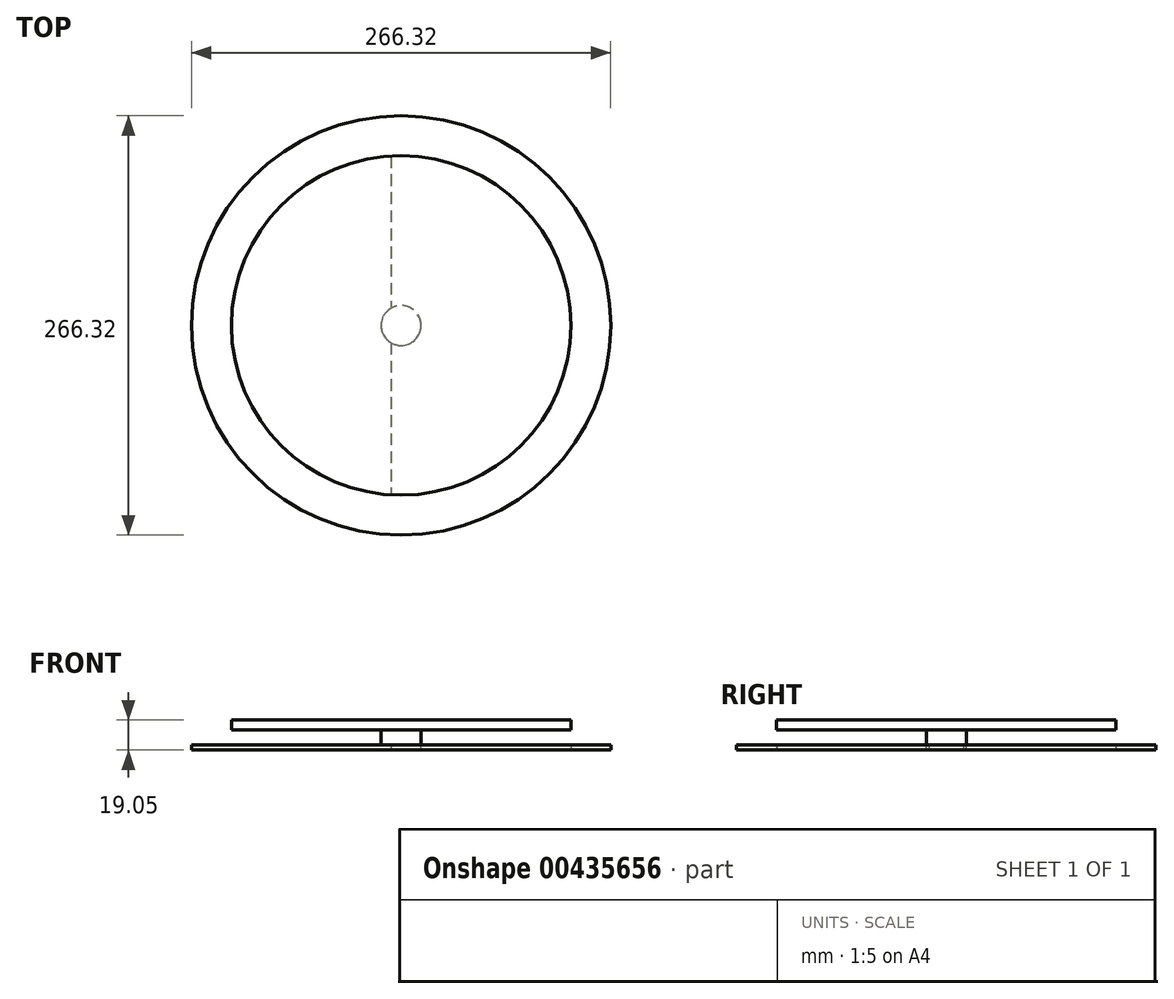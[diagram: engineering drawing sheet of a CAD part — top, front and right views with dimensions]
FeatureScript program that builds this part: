
annotation { "Feature Type Name" : "Feature", "Feature Type Description" : "" }
export const myFeature = defineFeature(function(context is Context, id is Id, definition is map)
    precondition{}
    {
        {
            var Q0;
            Q0=qCreatedBy(makeId("Top.planeOp"),FACE);
            var sketch = newSketch(context, id + "F0", { "sketchPlane" : qUnion([Q0])});
            skCircle(sketch, "E0", {"center": v(0, 0) * mm, "radius": 107.76 * mm});
            skCircle(sketch, "E1", {"center": v(0, 0) * mm, "radius": 12.7 * mm});
            skSolve(sketch);
        }
        {
            var Q0;
            Q0=makeQuery(id+"F0.imprint","IMPRINT",FACE,{"disambiguationData":[TD([[makeQuery(id+"F0.imprint","IMPRINT",EDGE,{"derivedFrom":sQuery(id+"F0.wireOp",EDGE,"E0")}),1.0]])]});
            var Q1;
            Q1=makeQuery(id+"F0.imprint","IMPRINT",FACE,{"disambiguationData":[TD([[makeQuery(id+"F0.imprint","IMPRINT",EDGE,{"derivedFrom":sQuery(id+"F0.wireOp",EDGE,"E1")}),1.0]])]});
            extrude(context, id + "F1", {"entities" : qUnion([Q0, Q1]), "depth" : 6.35 * mm});
        }
        {
            var Q0;
            Q0=makeQuery(id+"F0.imprint","IMPRINT",FACE,{"disambiguationData":[TD([[makeQuery(id+"F0.imprint","IMPRINT",EDGE,{"derivedFrom":sQuery(id+"F0.wireOp",EDGE,"E1")}),1.0]])]});
            extrude(context, id + "F2", {"entities" : qUnion([Q0]), "operationType" : NewBodyOperationType.ADD, "oppositeDirection" : true, "depth" : 12.7 * mm});
        }
        {
            var Q0;
            Q0=makeQuery(id+"F2.opExtrude","CAP_FACE",FACE,{"disambiguationData":[OSD([sQuery(id+"F0.wireOp",EDGE,"E1")])],"isStart":false});
            var sketch = newSketch(context, id + "F3", { "sketchPlane" : qUnion([Q0])});
            skCircle(sketch, "E2", {"center": v(0, 0) * mm, "radius": 107.76 * mm});
            skCircle(sketch, "E3.0", {"center": v(0, 0) * mm, "radius": 133.16 * mm});
            skLineSegment(sketch, "E4.bottom", {"start": v(6.35, -123.93) * mm, "end": v(-6.35, -123.93) * mm});
            skLineSegment(sketch, "E4.top", {"start": v(6.35, 123.93) * mm, "end": v(-6.35, 123.93) * mm});
            skLineSegment(sketch, "E4.left", {"start": v(6.35, -123.93) * mm, "end": v(6.35, 123.93) * mm});
            skLineSegment(sketch, "E4.right", {"start": v(-6.35, -123.93) * mm, "end": v(-6.35, 123.93) * mm});
            skSolve(sketch);
        }
        {
            var Q0;
            Q0=makeQuery(id+"F3.imprint","IMPRINT",FACE,{"disambiguationData":[TD([[makeQuery(id+"F3.imprint","IMPRINT",EDGE,{"derivedFrom":sQuery(id+"F3.wireOp",EDGE,"E2")}),-1.0]])]});
            var Q1;
            {var subQ0=sQuery(id+"F3.wireOp",EDGE,"E4.right");var subQ1=sQuery(id+"F3.wireOp",EDGE,"E2");var subQ2=makeQuery(id+"F3.imprint","INTERSECT",VERTEX,{"disambiguationData":[OD(1.0)],"derivedFrom":[subQ1,subQ0]});Q1=makeQuery(id+"F3.imprint","IMPRINT",FACE,{"disambiguationData":[TD([[makeQuery(id+"F3.imprint","IMPRINT",EDGE,{"disambiguationData":[TD([[subQ2,-1.0]])],"derivedFrom":subQ1}),1.0]])]});}
            var Q2;
            {var subQ0=sQuery(id+"F3.wireOp",EDGE,"E4.right");var subQ1=sQuery(id+"F3.wireOp",EDGE,"E2");var subQ2=makeQuery(id+"F3.imprint","INTERSECT",VERTEX,{"disambiguationData":[OD(0.0)],"derivedFrom":[subQ1,subQ0]});Q2=makeQuery(id+"F3.imprint","IMPRINT",FACE,{"disambiguationData":[TD([[makeQuery(id+"F3.imprint","IMPRINT",EDGE,{"disambiguationData":[TD([[subQ2,1.0]])],"derivedFrom":subQ1}),1.0]])]});}
            var Q3;
            {var subQ5=sQuery(id+"F3.wireOp",EDGE,"E4.bottom");Q3=makeQuery(id+"F3.imprint","IMPRINT",FACE,{"disambiguationData":[TD([[makeQuery(id+"F3.imprint","IMPRINT",EDGE,{"derivedFrom":subQ5}),-1.0]])]});}
            var Q4;
            {var subQ5=sQuery(id+"F3.wireOp",EDGE,"E4.top");Q4=makeQuery(id+"F3.imprint","IMPRINT",FACE,{"disambiguationData":[TD([[makeQuery(id+"F3.imprint","IMPRINT",EDGE,{"derivedFrom":subQ5}),1.0]])]});}
            extrude(context, id + "F4", {"entities" : qUnion([Q0, Q1, Q2, Q3, Q4]), "operationType" : NewBodyOperationType.ADD, "oppositeDirection" : true, "depth" : 3.17 * mm});
        }
    });
